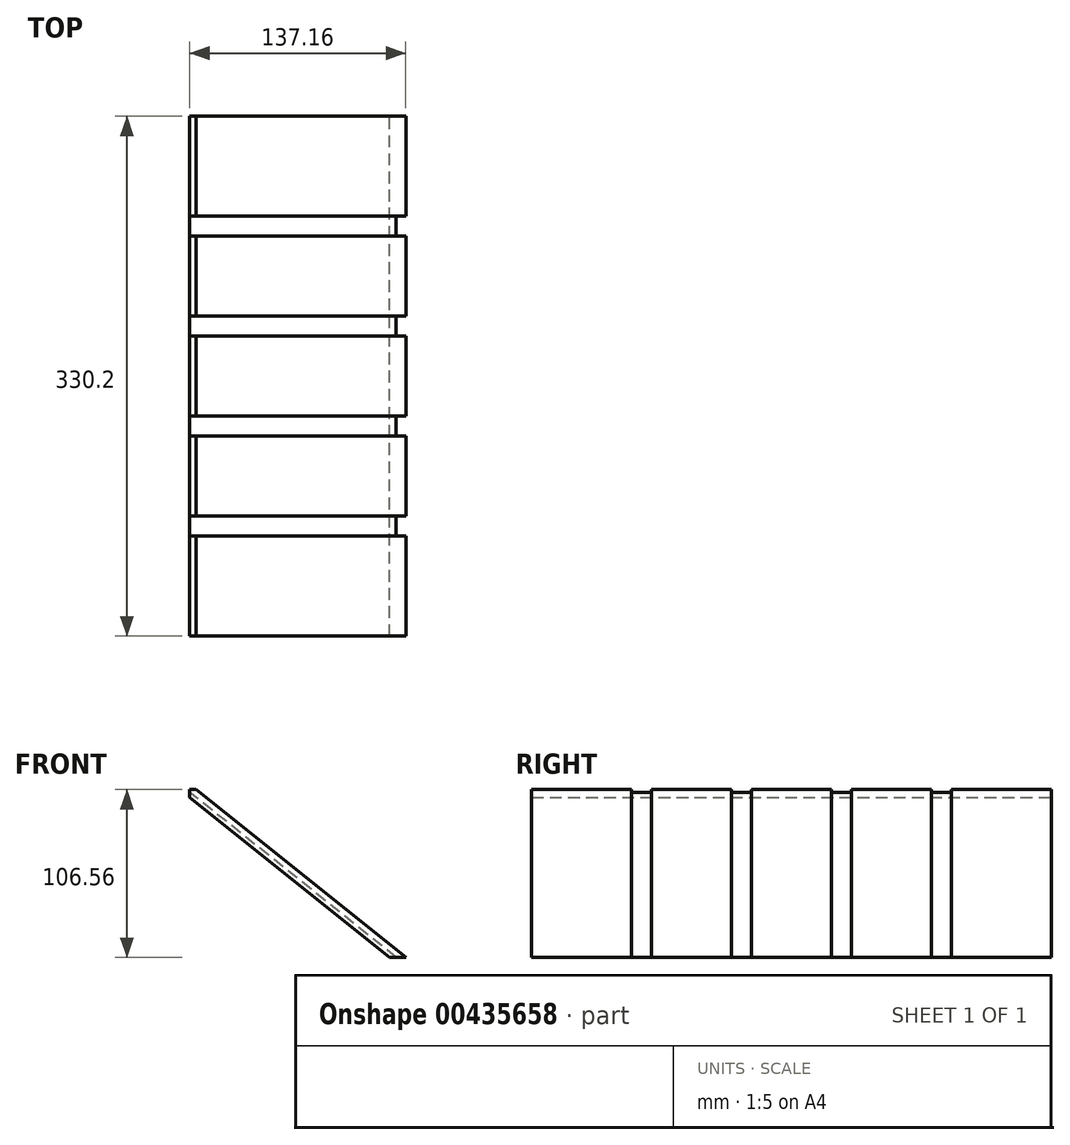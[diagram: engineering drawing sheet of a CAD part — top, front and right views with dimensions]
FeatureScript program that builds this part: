
annotation { "Feature Type Name" : "Feature", "Feature Type Description" : "" }
export const myFeature = defineFeature(function(context is Context, id is Id, definition is map)
    precondition{}
    {
        {
            var Q0;
            Q0=qCreatedBy(makeId("Front.planeOp"),FACE);
            var sketch = newSketch(context, id + "F0", { "sketchPlane" : qUnion([Q0])});
            skLineSegment(sketch, "E0", {"start": v(0, 0) * mm, "end": v(0, 101.6) * mm});
            skLineSegment(sketch, "E1", {"start": v(0, 0) * mm, "end": v(127, 0) * mm});
            skLineSegment(sketch, "E2", {"start": v(127, 0) * mm, "end": v(0, 101.6) * mm});
            skLineSegment(sketch, "E3.0", {"start": v(208.17, -56.8) * mm, "end": v(3.97, 106.56) * mm});
            skLineSegment(sketch, "E4", {"start": v(0, 106.56) * mm, "end": v(0, 101.6) * mm});
            skLineSegment(sketch, "E5", {"start": v(0, 106.56) * mm, "end": v(3.97, 106.56) * mm});
            skLineSegment(sketch, "E6", {"start": v(208.17, 0) * mm, "end": v(127, 0) * mm});
            skLineSegment(sketch, "E7", {"start": v(208.17, -56.8) * mm, "end": v(208.17, 0) * mm});
            skSolve(sketch);
        }
        {
            var Q0;
            Q0=makeQuery(id+"F0.imprint","IMPRINT",FACE,{"disambiguationData":[TD([[makeQuery(id+"F0.imprint","IMPRINT",EDGE,{"derivedFrom":sQuery(id+"F0.wireOp",EDGE,"E2")}),-1.0]])]});
            extrude(context, id + "F1", {"entities" : qUnion([Q0]), "depth" : 330.2 * mm});
        }
        {
            var Q0;
            Q0=makeQuery(id+"F1.opExtrude","SWEPT_FACE",FACE,{"disambiguationData":[OSD([sQuery(id+"F0.wireOp",EDGE,"E3.0")])]});
            var sketch = newSketch(context, id + "F2", { "sketchPlane" : qUnion([Q0])});
            skLineSegment(sketch, "E8", {"start": v(-63.47, -260.35) * mm, "end": v(107.1, -260.35) * mm});
            skLineSegment(sketch, "E9", {"start": v(-63.47, -69.85) * mm, "end": v(107.1, -69.85) * mm});
            skLineSegment(sketch, "E10", {"start": v(-63.47, -196.85) * mm, "end": v(107.1, -196.85) * mm});
            skLineSegment(sketch, "E11", {"start": v(-63.47, -133.35) * mm, "end": v(107.1, -133.35) * mm});
            skLineSegment(sketch, "E12.bottom", {"start": v(136.12, -254) * mm, "end": v(-92.48, -254) * mm});
            skLineSegment(sketch, "E12.top", {"start": v(136.12, -266.7) * mm, "end": v(-92.48, -266.7) * mm});
            skLineSegment(sketch, "E12.left", {"start": v(136.12, -254) * mm, "end": v(136.12, -266.7) * mm});
            skLineSegment(sketch, "E12.right", {"start": v(-92.48, -254) * mm, "end": v(-92.48, -266.7) * mm});
            skPoint(sketch, "E12.middle", {"position": v(21.82, -260.35) * mm});
            skLineSegment(sketch, "E13.bottom", {"start": v(136.12, -190.5) * mm, "end": v(-92.48, -190.5) * mm});
            skLineSegment(sketch, "E13.top", {"start": v(136.12, -203.2) * mm, "end": v(-92.48, -203.2) * mm});
            skLineSegment(sketch, "E13.left", {"start": v(136.12, -190.5) * mm, "end": v(136.12, -203.2) * mm});
            skLineSegment(sketch, "E13.right", {"start": v(-92.48, -190.5) * mm, "end": v(-92.48, -203.2) * mm});
            skPoint(sketch, "E13.middle", {"position": v(21.82, -196.85) * mm});
            skLineSegment(sketch, "E14.bottom", {"start": v(136.12, -127) * mm, "end": v(-92.48, -127) * mm});
            skLineSegment(sketch, "E14.top", {"start": v(136.12, -139.7) * mm, "end": v(-92.48, -139.7) * mm});
            skLineSegment(sketch, "E14.left", {"start": v(136.12, -127) * mm, "end": v(136.12, -139.7) * mm});
            skLineSegment(sketch, "E14.right", {"start": v(-92.48, -127) * mm, "end": v(-92.48, -139.7) * mm});
            skPoint(sketch, "E14.middle", {"position": v(21.82, -133.35) * mm});
            skLineSegment(sketch, "E15.bottom", {"start": v(136.12, -63.5) * mm, "end": v(-92.48, -63.5) * mm});
            skLineSegment(sketch, "E15.top", {"start": v(136.12, -76.2) * mm, "end": v(-92.48, -76.2) * mm});
            skLineSegment(sketch, "E15.left", {"start": v(136.12, -63.5) * mm, "end": v(136.12, -76.2) * mm});
            skLineSegment(sketch, "E15.right", {"start": v(-92.48, -63.5) * mm, "end": v(-92.48, -76.2) * mm});
            skPoint(sketch, "E15.middle", {"position": v(21.82, -69.85) * mm});
            skSolve(sketch);
        }
        {
            var Q0;
            Q0 = qSketchRegion(id + "F2", true);
            extrude(context, id + "F3", {"entities" : qUnion([Q0]), "operationType" : NewBodyOperationType.REMOVE, "oppositeDirection" : true, "depth" : 3.8 * mm});
        }
    });
